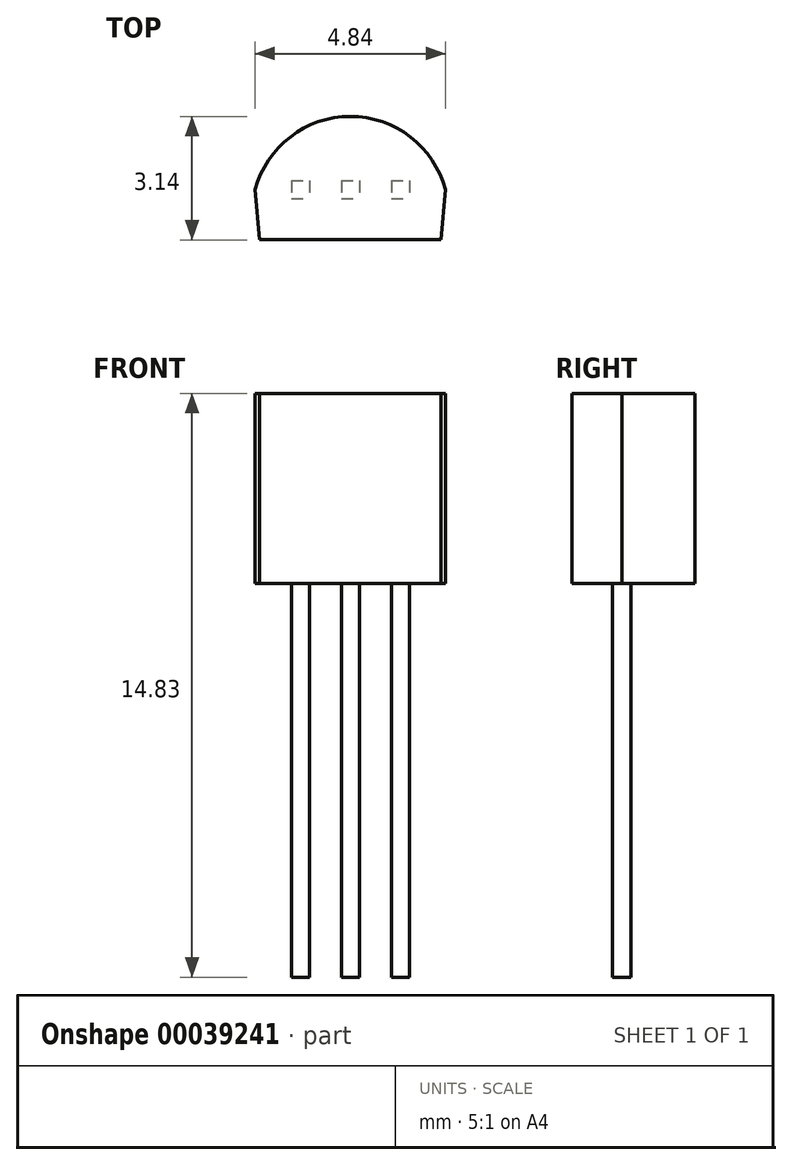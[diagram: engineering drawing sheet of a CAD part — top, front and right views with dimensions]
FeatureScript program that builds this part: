
annotation { "Feature Type Name" : "Feature", "Feature Type Description" : "" }
export const myFeature = defineFeature(function(context is Context, id is Id, definition is map)
    precondition{}
    {
        {
            var Q0;
            Q0=qCreatedBy(makeId("Top.planeOp"),FACE);
            var sketch = newSketch(context, id + "F0", { "sketchPlane" : qUnion([Q0])});
            skLineSegment(sketch, "E0", {"start": v(-23.57, 0) * mm, "end": v(29.55, 0) * mm, "construction": true});
            skPoint(sketch, "E1.rect.middle", {"position": v(0, 0) * mm});
            skPoint(sketch, "E1.rect.top.end.orphan", {"position": v(-2.42, -0.64) * mm});
            skPoint(sketch, "E1.rect.top.start.orphan", {"position": v(2.42, -0.64) * mm});
            skLineSegment(sketch, "E2", {"start": v(-2.41, 0.63) * mm, "end": v(-2.3, -0.64) * mm});
            skLineSegment(sketch, "E3", {"start": v(-2.3, -0.64) * mm, "end": v(2.3, -0.64) * mm});
            skLineSegment(sketch, "E4", {"start": v(2.3, -0.64) * mm, "end": v(2.41, 0.64) * mm});
            skArc(sketch, "E5", {"start": v(2.42, 0.64) * mm, "mid": v(0, 2.5) * mm, "end": v(-2.42, 0.63) * mm});
            skLineSegment(sketch, "E6", {"start": v(-2.41, 0.63) * mm, "end": v(2.41, 0.64) * mm, "construction": true});
            skSolve(sketch);
        }
        {
            var Q0;
            Q0 = qSketchRegion(id + "F0", true);
            extrude(context, id + "F1", {"entities" : qUnion([Q0]), "depth" : 4.83 * mm});
        }
        {
            var Q0;
            Q0=makeQuery(id+"F1.opExtrude","CAP_FACE",FACE,{"disambiguationData":[OSD([sQuery(id+"F0.wireOp",EDGE,"E2"),sQuery(id+"F0.wireOp",EDGE,"E3"),sQuery(id+"F0.wireOp",EDGE,"E4"),sQuery(id+"F0.wireOp",EDGE,"E5")])],"isStart":true});
            var sketch = newSketch(context, id + "F2", { "sketchPlane" : qUnion([Q0])});
            skLineSegment(sketch, "E7", {"start": v(2.42, -0.64) * mm, "end": v(-2.42, -0.63) * mm, "construction": true});
            skLineSegment(sketch, "E8.rect.bottom", {"start": v(-0.23, -0.86) * mm, "end": v(0.23, -0.86) * mm});
            skLineSegment(sketch, "E8.rect.top", {"start": v(-0.23, -0.4) * mm, "end": v(0.23, -0.4) * mm});
            skLineSegment(sketch, "E8.rect.left", {"start": v(-0.23, -0.86) * mm, "end": v(-0.23, -0.4) * mm});
            skLineSegment(sketch, "E8.rect.right", {"start": v(0.23, -0.86) * mm, "end": v(0.23, -0.4) * mm});
            skPoint(sketch, "E8.rect.middle", {"position": v(0, -0.63) * mm});
            skLineSegment(sketch, "E9.rect.bottom", {"start": v(1.04, -0.86) * mm, "end": v(1.5, -0.86) * mm});
            skLineSegment(sketch, "E9.rect.top", {"start": v(1.04, -0.4) * mm, "end": v(1.5, -0.4) * mm});
            skLineSegment(sketch, "E9.rect.left", {"start": v(1.04, -0.86) * mm, "end": v(1.04, -0.4) * mm});
            skLineSegment(sketch, "E9.rect.right", {"start": v(1.5, -0.86) * mm, "end": v(1.5, -0.4) * mm});
            skPoint(sketch, "E9.rect.middle", {"position": v(1.27, -0.63) * mm});
            skLineSegment(sketch, "E10.rect.bottom", {"start": v(-1.5, -0.86) * mm, "end": v(-1.04, -0.86) * mm});
            skLineSegment(sketch, "E10.rect.top", {"start": v(-1.5, -0.4) * mm, "end": v(-1.04, -0.4) * mm});
            skLineSegment(sketch, "E10.rect.left", {"start": v(-1.5, -0.86) * mm, "end": v(-1.5, -0.4) * mm});
            skLineSegment(sketch, "E10.rect.right", {"start": v(-1.04, -0.86) * mm, "end": v(-1.04, -0.4) * mm});
            skPoint(sketch, "E10.rect.middle", {"position": v(-1.27, -0.63) * mm});
            skSolve(sketch);
        }
        {
            var Q0;
            Q0 = qSketchRegion(id + "F2", true);
            extrude(context, id + "F3", {"entities" : qUnion([Q0]), "operationType" : NewBodyOperationType.ADD, "depth" : 10 * mm});
        }
    });
